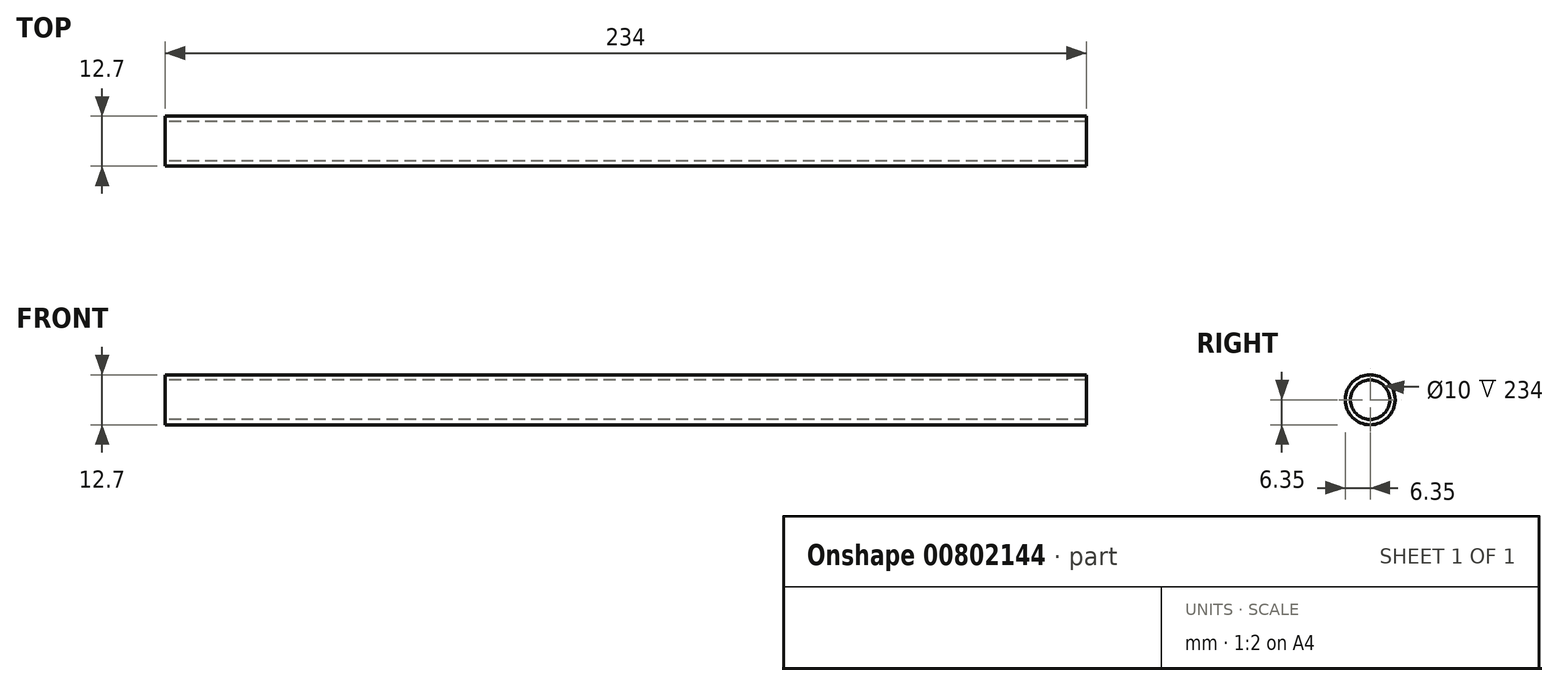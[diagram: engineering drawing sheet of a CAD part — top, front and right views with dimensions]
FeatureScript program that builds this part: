
annotation { "Feature Type Name" : "Feature", "Feature Type Description" : "" }
export const myFeature = defineFeature(function(context is Context, id is Id, definition is map)
    precondition{}
    {
        {
            var Q0;
            Q0=qCreatedBy(makeId("Right.planeOp"),FACE);
            var sketch = newSketch(context, id + "F0", { "sketchPlane" : qUnion([Q0])});
            skCircle(sketch, "E0", {"center": v(0, 0) * mm, "radius": 6.35 * mm});
            skCircle(sketch, "E1", {"center": v(0, 0) * mm, "radius": 5 * mm});
            skSolve(sketch);
        }
        {
            var Q0;
            Q0=qSketchRegion(id+"F0",true);
            extrude(context, id + "F1", {"entities" : qUnion([Q0]), "depth" : 234 * mm, "offsetDistance" : 25 * mm});
        }
    });
